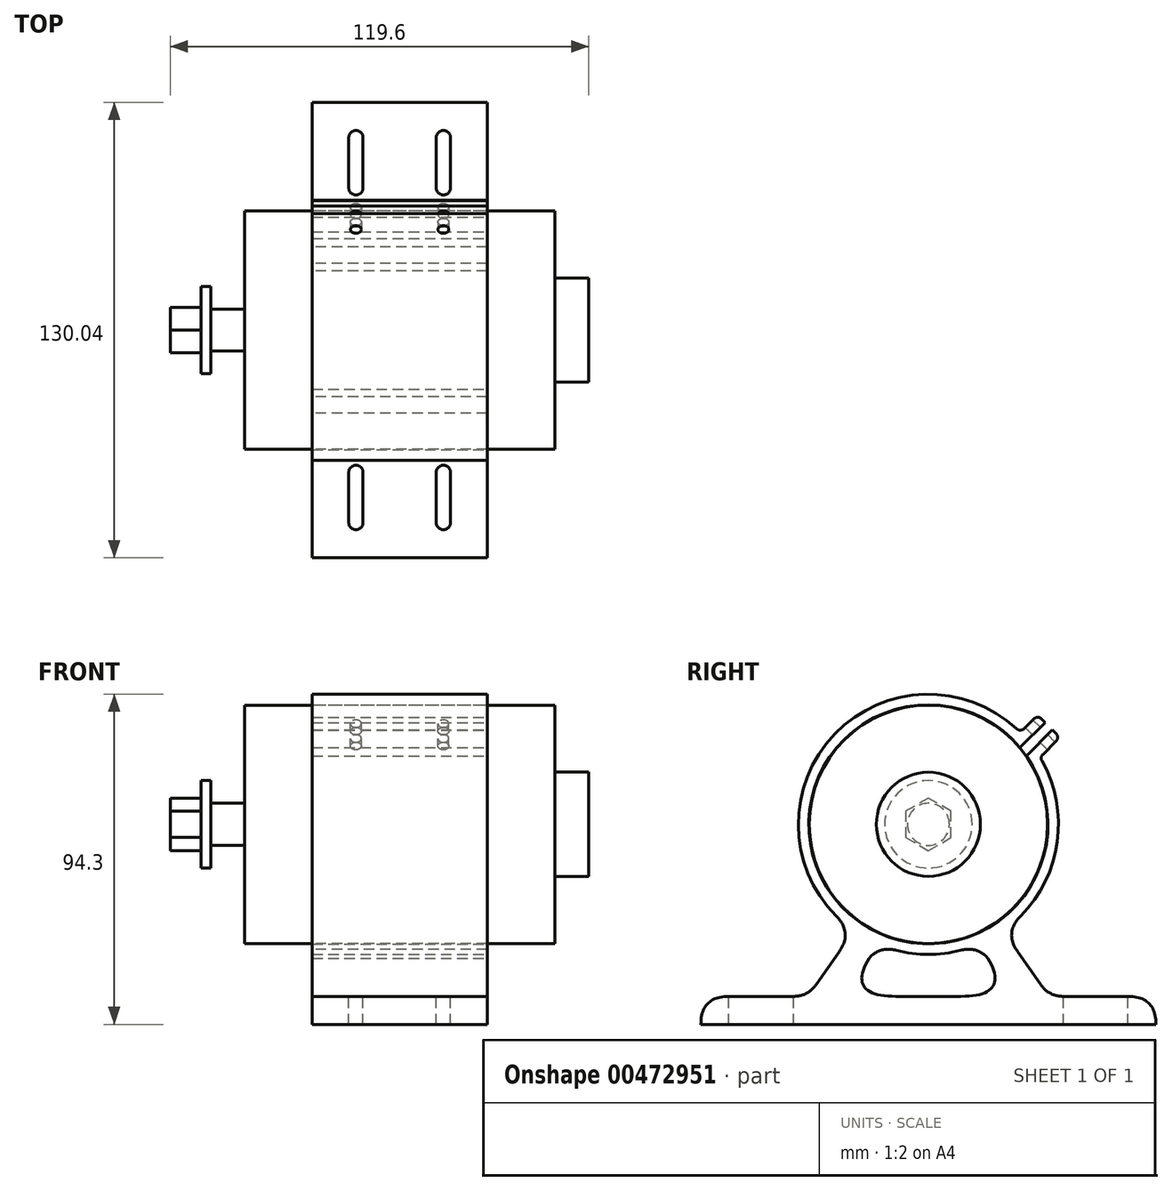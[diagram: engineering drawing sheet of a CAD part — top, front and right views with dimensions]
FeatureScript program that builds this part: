
annotation { "Feature Type Name" : "Feature", "Feature Type Description" : "" }
export const myFeature = defineFeature(function(context is Context, id is Id, definition is map)
    precondition{}
    {
        {
            var Q0;
            Q0=qCreatedBy(makeId("Right.planeOp"),FACE);
            var sketch = newSketch(context, id + "F0", { "sketchPlane" : qUnion([Q0])});
            skCircle(sketch, "E0", {"center": v(0, 0) * mm, "radius": 34.05 * mm});
            skArc(sketch, "E1", {"start": v(26.18, 21.93) * mm, "mid": v(-27.12, -20.75) * mm, "end": v(28.01, 19.53) * mm});
            skArc(sketch, "E2", {"start": v(26.27, 26.27) * mm, "mid": v(-28.46, 23.88) * mm, "end": v(-21.3, -30.43) * mm});
            skLineSegment(sketch, "E3", {"start": v(26.27, 26.27) * mm, "end": v(31.22, 31.22) * mm});
            skLineSegment(sketch, "E4", {"start": v(31.22, 31.22) * mm, "end": v(33.34, 29.1) * mm});
            skLineSegment(sketch, "E5", {"start": v(-21.3, -30.43) * mm, "end": v(-34.42, -49.15) * mm});
            skLineSegment(sketch, "E6", {"start": v(-40.02, -57.15) * mm, "end": v(40.02, -57.15) * mm});
            skLineSegment(sketch, "E7", {"start": v(34.42, -49.15) * mm, "end": v(21.3, -30.43) * mm});
            skLineSegment(sketch, "E8.0", {"start": v(24.65, -49.15) * mm, "end": v(14.26, -34.3) * mm});
            skLineSegment(sketch, "E8.1", {"start": v(-24.65, -49.15) * mm, "end": v(24.65, -49.15) * mm});
            skLineSegment(sketch, "E8.2", {"start": v(-14.26, -34.3) * mm, "end": v(-24.65, -49.15) * mm});
            skArc(sketch, "E9.trimOffspring", {"start": v(21.3, -30.43) * mm, "mid": v(36.34, -7.73) * mm, "end": v(31.85, 19.12) * mm});
            skArc(sketch, "E10.trimOffspring", {"start": v(-14.26, -34.3) * mm, "mid": v(0, -37.15) * mm, "end": v(14.26, -34.3) * mm});
            skLineSegment(sketch, "E11", {"start": v(40.02, -57.15) * mm, "end": v(65.02, -57.15) * mm});
            skLineSegment(sketch, "E12", {"start": v(65.02, -57.15) * mm, "end": v(65.02, -49.15) * mm});
            skLineSegment(sketch, "E13", {"start": v(65.02, -49.15) * mm, "end": v(34.42, -49.15) * mm});
            skLineSegment(sketch, "E14", {"start": v(-40.02, -57.15) * mm, "end": v(-65.02, -57.15) * mm});
            skLineSegment(sketch, "E15", {"start": v(-65.02, -57.15) * mm, "end": v(-65.02, -49.15) * mm});
            skLineSegment(sketch, "E16", {"start": v(-65.02, -49.15) * mm, "end": v(-34.42, -49.15) * mm});
            skLineSegment(sketch, "E17", {"start": v(0, -37.15) * mm, "end": v(0, -49.15) * mm, "construction": true});
            skLineSegment(sketch, "E18", {"start": v(35.45, 26.97) * mm, "end": v(37.56, 24.84) * mm});
            skLineSegment(sketch, "E19", {"start": v(31.85, 19.12) * mm, "end": v(37.56, 24.84) * mm});
            skLineSegment(sketch, "E20", {"start": v(35.45, 26.97) * mm, "end": v(28.01, 19.53) * mm});
            skLineSegment(sketch, "E21", {"start": v(26.18, 21.93) * mm, "end": v(33.34, 29.1) * mm});
            skSolve(sketch);
        }
        {
            var Q0;
            Q0=makeQuery(id+"F0.imprint","IMPRINT",FACE,{"disambiguationData":[TD([[makeQuery(id+"F0.imprint","IMPRINT",EDGE,{"derivedFrom":sQuery(id+"F0.wireOp",EDGE,"E0")}),1.0]])]});
            extrude(context, id + "F1", {"entities" : qUnion([Q0]), "depth" : 88.7 * mm, "offsetDistance" : 25 * mm, "symmetric" : true});
        }
        {
            var Q0;
            Q0=makeQuery(id+"F1.opExtrude","CAP_FACE",FACE,{"disambiguationData":[OSD([sQuery(id+"F0.wireOp",EDGE,"E0")])],"isStart":false});
            var sketch = newSketch(context, id + "F2", { "sketchPlane" : qUnion([Q0])});
            skCircle(sketch, "E22", {"center": v(0, 0) * mm, "radius": 14.88 * mm});
            skSolve(sketch);
        }
        {
            var Q0;
            Q0=makeQuery(id+"F2.imprint","IMPRINT",FACE,{"disambiguationData":[TD([[makeQuery(id+"F2.imprint","IMPRINT",EDGE,{"derivedFrom":sQuery(id+"F2.wireOp",EDGE,"E22")}),1.0]])]});
            var Q1;
            Q1=sQuery(id+"F2.wireOp",EDGE,"E22");
            extrude(context, id + "F3", {"entities" : qUnion([Q0]), "operationType" : NewBodyOperationType.ADD, "surfaceEntities" : qUnion([Q1]), "depth" : 9.7 * mm, "offsetDistance" : 25 * mm});
        }
        {
            var Q0;
            Q0=makeQuery(id+"F1.opExtrude","CAP_FACE",FACE,{"disambiguationData":[OSD([sQuery(id+"F0.wireOp",EDGE,"E0")])],"isStart":true});
            var sketch = newSketch(context, id + "F4", { "sketchPlane" : qUnion([Q0])});
            skCircle(sketch, "E23", {"center": v(0, 0) * mm, "radius": 6 * mm});
            skSolve(sketch);
        }
        {
            var Q0;
            Q0 = qSketchRegion(id + "F4", true);
            extrude(context, id + "F5", {"entities" : qUnion([Q0]), "operationType" : NewBodyOperationType.ADD, "depth" : (21.2 - 8.85 - 2.8) * mm, "offsetDistance" : 25 * mm});
        }
        {
            var Q0;
            Q0=makeQuery(id+"F5.opExtrude","CAP_FACE",FACE,{"disambiguationData":[OSD([sQuery(id+"F4.wireOp",EDGE,"E23")])],"isStart":false});
            var sketch = newSketch(context, id + "F6", { "sketchPlane" : qUnion([Q0])});
            skCircle(sketch, "E24", {"center": v(0, 0) * mm, "radius": 12.5 * mm});
            skSolve(sketch);
        }
        {
            var Q0;
            Q0 = qSketchRegion(id + "F6", true);
            extrude(context, id + "F7", {"entities" : qUnion([Q0]), "depth" : 2.8 * mm, "offsetDistance" : 25 * mm});
        }
        {
            var Q0;
            Q0=makeQuery(id+"F7.opExtrude","CAP_FACE",FACE,{"disambiguationData":[OSD([sQuery(id+"F6.wireOp",EDGE,"E24")])],"isStart":false});
            var sketch = newSketch(context, id + "F8", { "sketchPlane" : qUnion([Q0])});
            skCircle(sketch, "E25.cCircle", {"center": v(0, 0) * mm, "radius": 6.5 * mm, "construction": true});
            skLineSegment(sketch, "E25.0", {"start": v(0, 7.5) * mm, "end": v(6.5, 3.75) * mm});
            skLineSegment(sketch, "E25.1", {"start": v(6.5, 3.75) * mm, "end": v(6.5, -3.75) * mm});
            skLineSegment(sketch, "E25.2", {"start": v(6.5, -3.75) * mm, "end": v(0, -7.5) * mm});
            skLineSegment(sketch, "E25.3", {"start": v(0, -7.5) * mm, "end": v(-6.5, -3.75) * mm});
            skLineSegment(sketch, "E25.4", {"start": v(-6.5, -3.75) * mm, "end": v(-6.5, 3.75) * mm});
            skLineSegment(sketch, "E25.5", {"start": v(-6.5, 3.75) * mm, "end": v(0, 7.5) * mm});
            skPoint(sketch, "E25.0.midPoint", {"position": v(3.25, 5.63) * mm});
            skSolve(sketch);
        }
        {
            var Q0;
            Q0 = qSketchRegion(id + "F8", true);
            extrude(context, id + "F9", {"entities" : qUnion([Q0]), "operationType" : NewBodyOperationType.ADD, "depth" : 8.85 * mm, "offsetDistance" : 25 * mm});
        }
        {
            var Q0;
            Q0=makeQuery(id+"F0.imprint","IMPRINT",FACE,{"disambiguationData":[TD([[makeQuery(id+"F0.imprint","IMPRINT",EDGE,{"derivedFrom":sQuery(id+"F0.wireOp",EDGE,"E1")}),-1.0]])]});
            extrude(context, id + "F10", {"entities" : qUnion([Q0]), "oppositeDirection" : true, "depth" : 50 * mm, "offsetDistance" : 25 * mm, "symmetric" : true});
        }
        {
            var Q0;
            Q0=makeQuery(id+"F10.opExtrude","SWEPT_EDGE",EDGE,{"disambiguationData":[OSD([sQuery(id+"F0.wireOp",EDGE,"E7"),sQuery(id+"F0.wireOp",EDGE,"E13")])]});
            var Q1;
            Q1=makeQuery(id+"F10.opExtrude","SWEPT_EDGE",EDGE,{"disambiguationData":[OSD([sQuery(id+"F0.wireOp",EDGE,"E5"),sQuery(id+"F0.wireOp",EDGE,"E16")])]});
            var Q2;
            Q2=makeQuery(id+"F10.opExtrude","SWEPT_EDGE",EDGE,{"disambiguationData":[OSD([sQuery(id+"F0.wireOp",EDGE,"E2"),sQuery(id+"F0.wireOp",EDGE,"E5")])]});
            var Q3;
            Q3=makeQuery(id+"F10.opExtrude","SWEPT_EDGE",EDGE,{"disambiguationData":[OSD([sQuery(id+"F0.wireOp",EDGE,"E8.1"),sQuery(id+"F0.wireOp",EDGE,"E8.2")])]});
            var Q4;
            Q4=makeQuery(id+"F10.opExtrude","SWEPT_EDGE",EDGE,{"disambiguationData":[OSD([sQuery(id+"F0.wireOp",EDGE,"E8.0"),sQuery(id+"F0.wireOp",EDGE,"E8.1")])]});
            var Q5;
            Q5=makeQuery(id+"F10.opExtrude","SWEPT_EDGE",EDGE,{"disambiguationData":[OSD([sQuery(id+"F0.wireOp",EDGE,"E8.0"),sQuery(id+"F0.wireOp",EDGE,"E10.trimOffspring")])]});
            var Q6;
            Q6=makeQuery(id+"F10.opExtrude","SWEPT_EDGE",EDGE,{"disambiguationData":[OSD([sQuery(id+"F0.wireOp",EDGE,"E7"),sQuery(id+"F0.wireOp",EDGE,"E9.trimOffspring")])]});
            var Q7;
            Q7=makeQuery(id+"F10.opExtrude","SWEPT_EDGE",EDGE,{"disambiguationData":[OSD([sQuery(id+"F0.wireOp",EDGE,"E8.2"),sQuery(id+"F0.wireOp",EDGE,"E10.trimOffspring")])]});
            var Q8;
            Q8=makeQuery(id+"F10.opExtrude","SWEPT_EDGE",EDGE,{"disambiguationData":[OSD([sQuery(id+"F0.wireOp",EDGE,"E15"),sQuery(id+"F0.wireOp",EDGE,"E16")])]});
            var Q9;
            Q9=makeQuery(id+"F10.opExtrude","SWEPT_EDGE",EDGE,{"disambiguationData":[OSD([sQuery(id+"F0.wireOp",EDGE,"E12"),sQuery(id+"F0.wireOp",EDGE,"E13")])]});
            fillet(context, id + "F11", {"entities" : qUnion([Q0, Q1, Q2, Q3, Q4, Q5, Q6, Q7, Q8, Q9]), "radius" : 8 * mm, "tangentPropagation" : true, "rho" : 0.5, "crossSection" : FilletCrossSection.CONIC, "allowEdgeOverflow" : false});
        }
        {
            var Q0;
            Q0=makeQuery(id+"F10.opExtrude","SWEPT_FACE",FACE,{"disambiguationData":[OSD([sQuery(id+"F0.wireOp",EDGE,"E13")])]});
            var sketch = newSketch(context, id + "F12", { "sketchPlane" : qUnion([Q0])});
            skFitSpline(sketch, "E26.0", {"points": [v(25, 57.65) * mm, v(8.33, 57.65) * mm, v(-8.33, 57.65) * mm, v(-25, 57.65) * mm], "construction": true});
            skFitSpline(sketch, "E27.0", {"points": [v(-25, 39.2) * mm, v(-8.33, 39.2) * mm, v(8.33, 39.2) * mm, v(25, 39.2) * mm], "construction": true});
            skLineSegment(sketch, "E28.0", {"start": v(-25, 57.02) * mm, "end": v(-25, 38.58) * mm, "construction": true});
            skLineSegment(sketch, "E29.0", {"start": v(25, 57.02) * mm, "end": v(25, 38.58) * mm});
            skLineSegment(sketch, "E30", {"start": v(0, 57.02) * mm, "end": v(0, 38.58) * mm, "construction": true});
            skPoint(sketch, "E30.endSnap0", {"position": v(0, 47.8) * mm});
            skPoint(sketch, "E31", {"position": v(0, 57.02) * mm});
            skPoint(sketch, "E32", {"position": v(0, 38.58) * mm});
            skLineSegment(sketch, "E33", {"start": v(-25, 47.8) * mm, "end": v(0, 47.8) * mm, "construction": true});
            skLineSegment(sketch, "E34", {"start": v(0, 47.8) * mm, "end": v(25, 47.8) * mm, "construction": true});
            skLineSegment(sketch, "E35", {"start": v(-12.5, 47.8) * mm, "end": v(-12.5, 38.58) * mm});
            skLineSegment(sketch, "E36", {"start": v(-12.5, 38.58) * mm, "end": v(-12.5, 57.02) * mm, "construction": true});
            skLineSegment(sketch, "E37", {"start": v(12.5, 47.8) * mm, "end": v(12.5, 38.58) * mm});
            skLineSegment(sketch, "E38", {"start": v(12.5, 38.58) * mm, "end": v(12.5, 57.02) * mm, "construction": true});
            skFitSpline(sketch, "E39.0", {"points": [v(25, -39.2) * mm, v(8.33, -39.2) * mm, v(-8.33, -39.2) * mm, v(-25, -39.2) * mm], "construction": true});
            skLineSegment(sketch, "E40.0.0", {"start": v(25, -57.02) * mm, "end": v(25, -38.58) * mm, "construction": true});
            skLineSegment(sketch, "E40.0.2", {"start": v(-25, -38.58) * mm, "end": v(-25, -57.02) * mm, "construction": true});
            skLineSegment(sketch, "E41", {"start": v(0, -57.02) * mm, "end": v(0, -38.58) * mm, "construction": true});
            skLineSegment(sketch, "E42", {"start": v(-25, -47.8) * mm, "end": v(0, -47.8) * mm, "construction": true});
            skLineSegment(sketch, "E43", {"start": v(0, -47.8) * mm, "end": v(25, -47.8) * mm, "construction": true});
            skLineSegment(sketch, "E44", {"start": v(25, -57.02) * mm, "end": v(0, -57.02) * mm, "construction": true});
            skLineSegment(sketch, "E45", {"start": v(-25, -57.02) * mm, "end": v(0, -57.02) * mm, "construction": true});
            skLineSegment(sketch, "E46", {"start": v(12.5, -57.02) * mm, "end": v(12.5, -38.58) * mm, "construction": true});
            skPoint(sketch, "E46.endSnap0", {"position": v(12.5, -47.8) * mm});
            skLineSegment(sketch, "E47", {"start": v(-12.5, -57.02) * mm, "end": v(-12.5, -38.58) * mm, "construction": true});
            skCircle(sketch, "E48", {"center": v(-12.5, 57.02) * mm, "radius": 2.05 * mm, "construction": true});
            skCircle(sketch, "E49", {"center": v(-12.5, 38.58) * mm, "radius": 2.05 * mm, "construction": true});
            skArc(sketch, "E50", {"start": v(-10.45, 54.97) * mm, "mid": v(-12.5, 57.02) * mm, "end": v(-14.55, 54.97) * mm});
            skArc(sketch, "E51", {"start": v(-14.55, 40.63) * mm, "mid": v(-12.5, 38.58) * mm, "end": v(-10.45, 40.63) * mm});
            skLineSegment(sketch, "E52", {"start": v(-10.45, 54.97) * mm, "end": v(-10.45, 40.63) * mm});
            skLineSegment(sketch, "E53", {"start": v(-14.55, 54.97) * mm, "end": v(-14.55, 40.63) * mm});
            skArc(sketch, "E54", {"start": v(10.45, 57.02) * mm, "mid": v(12.5, 54.97) * mm, "end": v(14.55, 57.02) * mm, "construction": true});
            skArc(sketch, "E55", {"start": v(14.55, 38.58) * mm, "mid": v(12.5, 40.63) * mm, "end": v(10.45, 38.58) * mm, "construction": true});
            skArc(sketch, "E56", {"start": v(14.55, 54.97) * mm, "mid": v(12.5, 57.02) * mm, "end": v(10.45, 54.97) * mm});
            skArc(sketch, "E57", {"start": v(10.45, 40.63) * mm, "mid": v(12.5, 38.58) * mm, "end": v(14.55, 40.63) * mm});
            skLineSegment(sketch, "E58", {"start": v(14.55, 54.97) * mm, "end": v(14.55, 40.63) * mm});
            skLineSegment(sketch, "E59", {"start": v(10.45, 54.97) * mm, "end": v(10.45, 40.63) * mm});
            skArc(sketch, "E60", {"start": v(-14.55, -38.58) * mm, "mid": v(-12.5, -40.63) * mm, "end": v(-10.45, -38.58) * mm, "construction": true});
            skArc(sketch, "E61", {"start": v(-10.45, -57.02) * mm, "mid": v(-12.5, -54.97) * mm, "end": v(-14.55, -57.02) * mm, "construction": true});
            skArc(sketch, "E62", {"start": v(-10.45, -40.63) * mm, "mid": v(-12.5, -38.58) * mm, "end": v(-14.55, -40.63) * mm});
            skArc(sketch, "E63", {"start": v(-14.55, -54.97) * mm, "mid": v(-12.5, -57.02) * mm, "end": v(-10.45, -54.97) * mm});
            skLineSegment(sketch, "E64", {"start": v(-10.45, -40.63) * mm, "end": v(-10.45, -54.97) * mm});
            skLineSegment(sketch, "E65", {"start": v(-14.55, -40.63) * mm, "end": v(-14.55, -54.97) * mm});
            skPoint(sketch, "E66.center.orphan", {"position": v(-12.5, -47.8) * mm});
            skArc(sketch, "E67", {"start": v(10.45, -38.58) * mm, "mid": v(12.5, -40.63) * mm, "end": v(14.55, -38.58) * mm, "construction": true});
            skArc(sketch, "E68", {"start": v(14.55, -57.02) * mm, "mid": v(12.5, -54.97) * mm, "end": v(10.45, -57.02) * mm, "construction": true});
            skArc(sketch, "E69", {"start": v(14.55, -40.63) * mm, "mid": v(12.5, -38.58) * mm, "end": v(10.45, -40.63) * mm});
            skArc(sketch, "E70", {"start": v(10.45, -54.97) * mm, "mid": v(12.5, -57.02) * mm, "end": v(14.55, -54.97) * mm});
            skLineSegment(sketch, "E71", {"start": v(14.55, -40.63) * mm, "end": v(14.55, -54.97) * mm});
            skLineSegment(sketch, "E72", {"start": v(10.45, -40.63) * mm, "end": v(10.45, -54.97) * mm});
            skSolve(sketch);
        }
        {
            var Q0;
            {var subQ4=sQuery(id+"F12.wireOp",EDGE,"E52");Q0=makeQuery(id+"F12.imprint","IMPRINT",FACE,{"disambiguationData":[TD([[makeQuery(id+"F12.imprint","IMPRINT",EDGE,{"derivedFrom":subQ4}),-1.0]])]});}
            var Q1;
            {var subQ4=sQuery(id+"F12.wireOp",EDGE,"E58");Q1=makeQuery(id+"F12.imprint","IMPRINT",FACE,{"disambiguationData":[TD([[makeQuery(id+"F12.imprint","IMPRINT",EDGE,{"derivedFrom":subQ4}),-1.0]])]});}
            var Q2;
            Q2=makeQuery(id+"F12.imprint","IMPRINT",FACE,{"disambiguationData":[TD([[makeQuery(id+"F12.imprint","IMPRINT",EDGE,{"derivedFrom":sQuery(id+"F12.wireOp",EDGE,"E69")}),1.0]])]});
            var Q3;
            Q3=makeQuery(id+"F12.imprint","IMPRINT",FACE,{"disambiguationData":[TD([[makeQuery(id+"F12.imprint","IMPRINT",EDGE,{"derivedFrom":sQuery(id+"F12.wireOp",EDGE,"E62")}),1.0]])]});
            extrude(context, id + "F13", {"entities" : qUnion([Q0, Q1, Q2, Q3]), "operationType" : NewBodyOperationType.REMOVE, "endBound" : BoundingType.THROUGH_ALL, "oppositeDirection" : true, "depth" : 25 * mm, "offsetDistance" : 25 * mm});
        }
        {
            var Q0;
            Q0=makeQuery(id+"F10.opExtrude","SWEPT_FACE",FACE,{"disambiguationData":[OSD([sQuery(id+"F0.wireOp",EDGE,"E3")])]});
            var sketch = newSketch(context, id + "F14", { "sketchPlane" : qUnion([Q0])});
            skLineSegment(sketch, "E73.0", {"start": v(-25, 44.15) * mm, "end": v(25, 44.15) * mm, "construction": true});
            skLineSegment(sketch, "E74.0", {"start": v(25, 37.15) * mm, "end": v(25, 44.15) * mm, "construction": true});
            skLineSegment(sketch, "E75.0", {"start": v(-25, 37.15) * mm, "end": v(-25, 44.15) * mm, "construction": true});
            skLineSegment(sketch, "E76.0", {"start": v(-25, 37.15) * mm, "end": v(25, 37.15) * mm, "construction": true});
            skLineSegment(sketch, "E77", {"start": v(0, 44.15) * mm, "end": v(0, 37.15) * mm, "construction": true});
            skLineSegment(sketch, "E78", {"start": v(0, 40.65) * mm, "end": v(25, 40.65) * mm, "construction": true});
            skLineSegment(sketch, "E79", {"start": v(0, 40.65) * mm, "end": v(-25, 40.65) * mm, "construction": true});
            skCircle(sketch, "E80", {"center": v(12.5, 40.65) * mm, "radius": 1.55 * mm});
            skCircle(sketch, "E81", {"center": v(-12.5, 40.65) * mm, "radius": 1.55 * mm});
            skSolve(sketch);
        }
        {
            var Q0;
            Q0=makeQuery(id+"F14.imprint","IMPRINT",FACE,{"disambiguationData":[TD([[makeQuery(id+"F14.imprint","IMPRINT",EDGE,{"derivedFrom":sQuery(id+"F14.wireOp",EDGE,"E81")}),1.0]])]});
            var Q1;
            Q1=makeQuery(id+"F14.imprint","IMPRINT",FACE,{"disambiguationData":[TD([[makeQuery(id+"F14.imprint","IMPRINT",EDGE,{"derivedFrom":sQuery(id+"F14.wireOp",EDGE,"E80")}),1.0]])]});
            var Q2;
            Q2=sQuery(id+"F14.wireOp",EDGE,"E81");
            var Q3;
            Q3=sQuery(id+"F14.wireOp",EDGE,"E80");
            extrude(context, id + "F15", {"entities" : qUnion([Q0, Q1]), "operationType" : NewBodyOperationType.REMOVE, "surfaceEntities" : qUnion([Q2, Q3]), "endBound" : BoundingType.THROUGH_ALL, "oppositeDirection" : true, "depth" : 25 * mm, "offsetDistance" : 25 * mm});
        }
        {
            var Q0;
            Q0=makeQuery(id+"F10.opExtrude","SWEPT_EDGE",EDGE,{"disambiguationData":[OSD([sQuery(id+"F0.wireOp",EDGE,"E3"),sQuery(id+"F0.wireOp",EDGE,"E4")])]});
            var Q1;
            Q1=makeQuery(id+"F10.opExtrude","SWEPT_EDGE",EDGE,{"disambiguationData":[OSD([sQuery(id+"F0.wireOp",EDGE,"E18"),sQuery(id+"F0.wireOp",EDGE,"E19")])]});
            var Q2;
            Q2=makeQuery(id+"F10.opExtrude","SWEPT_EDGE",EDGE,{"disambiguationData":[OSD([sQuery(id+"F0.wireOp",EDGE,"E9.trimOffspring"),sQuery(id+"F0.wireOp",EDGE,"E19")])]});
            var Q3;
            Q3=makeQuery(id+"F10.opExtrude","SWEPT_EDGE",EDGE,{"disambiguationData":[OSD([sQuery(id+"F0.wireOp",EDGE,"E2"),sQuery(id+"F0.wireOp",EDGE,"E3")])]});
            fillet(context, id + "F16", {"entities" : qUnion([Q0, Q1, Q2, Q3]), "radius" : 1.5 * mm, "tangentPropagation" : true, "allowEdgeOverflow" : false});
        }
    });
